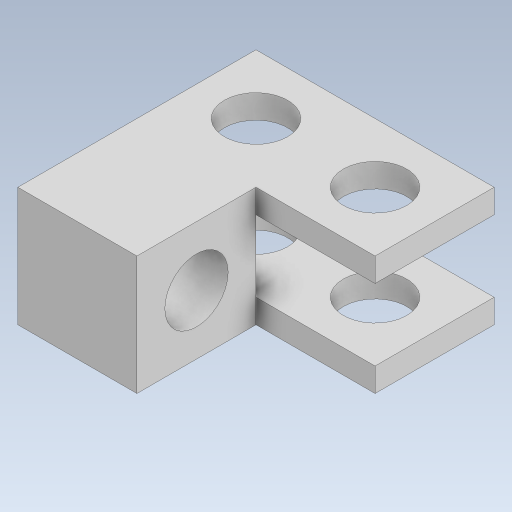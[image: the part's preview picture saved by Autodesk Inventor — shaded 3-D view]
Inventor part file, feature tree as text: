
AUTODESK INVENTOR PART (.ipt)
format: ipt  version: 2023 (Build 270158000, 158)  size: 152,064 bytes
history: native  units: in
note: dims shown in document units (in); Inventor stores cm internally (conversion verified against a paired STEP export)
features: sketch x4, extrude x2, hole x2, plane x1
ambient origin geometry x8: Origin, YZ Plane, XZ Plane, XY Plane, X Axis, Y Axis, Z Axis, Center Point
bodies: Solid1 (feature_tree)
feature tree (9):
  extrude  "Extrusion1"  Depth=1.0in
  sketch  "Sketch2"  dims[d2=1.0in d3=0.5in]
  extrude  "Extrusion2"  Depth=0.5in
  hole  "Hole2"  [1 undecoded]
  hole  "Hole3"  [1 undecoded]
  plane  "Work Plane1"
  sketch  "Sketch1"  dims[d0=0.5in d1=1.0in]
  sketch  "Sketch3"  dims[d4=0.5in d5=0.0in d6=0.25in]
  sketch  "Sketch4"  dims[d15=0.3in d16=0.5in d17=0.0in d18=0.266in d19=0.75in d20=0.375in d21=0.25in d22=0.5635in d23=0.5in d24=0.8108in d25=0.266in d26=0.75in d27=0.375in d28=0.25in d29=0.5635in d30=0.5in d31=0.8108in d32=-0.25in]
note: 2 required parameter values undecoded (feature->parameter linkage not recoverable at this tier; creation-order binding heuristic only, values carry confidence <= 0.55)
